# Revit family: LPD
name_source: partatom
category: Mechanical Equipment
units: mm (PartAtom-declared; Revit-internal decimal feet)

## family parameters
Always vertical = Yes
Cut with Voids When Loaded = No
Part Type = Normal
Room Calculation Point = No
Round Connector Dimension = Use Diameter
Shared = No
Work Plane-Based = No

## types (5) — shared parameters
0 = 0' - 0"
1" = 0' - 1"
1.5 = 0' - 1 1/2"
2" = 0' - 2"
2' = 2' - 0"
3" = 0' - 3"
4" = 0' - 4"
G = 0' - 2"
G-.125" = 0' - 1 7/8"
Manufacturer = Loren Cook Company
Model = LPD
ONE EIGTH = 0' - 0 1/8"
Type Comments = Low Profile Centrifugal Exhaust Ventilator Roof Mounted/Direct Drive
URL = www.lorencook.com

## per-type parameters (varying)
| type | (F-B)/2 | -(D+1") | A | A/2 | B | B/2 | C | C+G | C/2 | D | E | F | F/2 | H | I | J | RO | RO/2 | T_SQ | T_SQ/2 |
| 100_LPD | 0' - 11 5/32" | -0' - 7 11/16" | 1' - 10 1/16" | 0' - 11 1/32" | 2' - 5 7/8" | 1' - 2 15/16" | 1' - 1 7/8" | 1' - 3 7/8" | 0' - 6 15/16" | 0' - 6 11/16" | 0' - 6 25/32" | 4' - 4 3/16" | 2' - 2 3/32" | 0' - 1 1/32" | 0' - 8 19/32" | 0' - 1 9/32" | 1' - 3 1/2" | 0' - 7 3/4" | 1' - 8" | 0' - 10" |
| 120_LPD | 1' - 1 7/32" | -0' - 9" | 2' - 1 11/16" | 1' - 0 27/32" | 2' - 8 3/8" | 1' - 4 3/16" | 1' - 3 3/8" | 1' - 5 3/8" | 0' - 7 11/16" | 0' - 8" | 0' - 8 5/32" | 4' - 10 13/16" | 2' - 5 13/32" | 0' - 0 27/32" | 0' - 7 29/32" | 0' - 0 15/32" | 1' - 7 1/2" | 0' - 9 3/4" | 2' - 0" | 1' - 0" |
| 135_LPD | 1' - 2 13/16" | -0' - 10" | 2' - 4 7/16" | 1' - 2 7/32" | 2' - 10 1/2" | 1' - 5 1/4" | 1' - 4 3/8" | 1' - 6 3/8" | 0' - 8 3/16" | 0' - 9" | 0' - 9 3/16" | 5' - 4 1/8" | 2' - 8 1/16" | 0' - 2 7/32" | 0' - 8 15/16" | 0' - 1 9/16" | 1' - 7 1/2" | 0' - 9 3/4" | 2' - 0" | 1' - 0" |
| 150_LPD | 1' - 4 11/32" | -0' - 11" | 2' - 7 1/8" | 1' - 3 9/16" | 3' - 0 11/16" | 1' - 6 11/32" | 1' - 5 3/8" | 1' - 7 3/8" | 0' - 8 11/16" | 0' - 10" | 0' - 10 7/32" | 5' - 9 3/8" | 2' - 10 11/16" | 0' - 3 9/16" | 0' - 9 15/16" | 0' - 2 3/4" | 1' - 7 1/2" | 0' - 9 3/4" | 2' - 0" | 1' - 0" |
| 165_LPD | 1' - 5 27/32" | -1' - 0" | 2' - 9 13/16" | 1' - 4 29/32" | 3' - 3" | 1' - 7 1/2" | 1' - 6 3/8" | 1' - 8 3/8" | 0' - 9 3/16" | 0' - 11" | 0' - 11 7/32" | 6' - 2 11/16" | 3' - 1 11/32" | 0' - 4 29/32" | 0' - 10 15/16" | 0' - 4 1/16" | 1' - 7 1/2" | 0' - 9 3/4" | 2' - 0" | 1' - 0" |

## geometry (parser evidence)
native form markers: Sweep x2
no freeform markers — native parametric forms only
